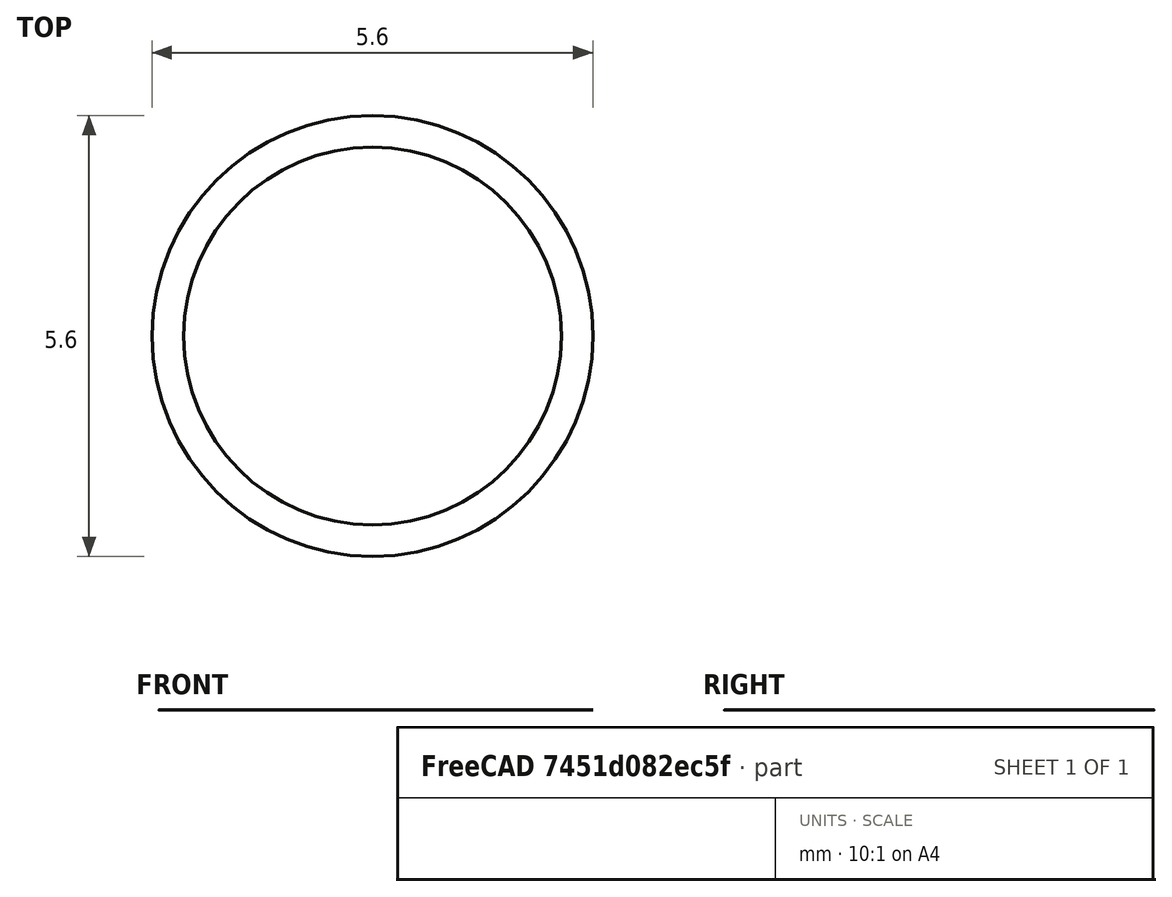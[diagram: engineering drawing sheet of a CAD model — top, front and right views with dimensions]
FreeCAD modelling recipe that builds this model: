
FCSTD DOCUMENT  (FreeCAD 0.20R29603 (Git))
Label: nested_coax
License: All rights reserved
LicenseURL: http://en.wikipedia.org/wiki/All_rights_reserved
objects: Part::Part2DObjectPython×4, App::FeaturePython×4, Part::Cut×1
note: 5 computed .brp shape members not serialized (recipe doc carries the construction recipe); baked Part::Feature solids carry a one-line shape summary decoded from their .brp

FEATURE [Part::Part2DObjectPython] Circle  label="Conductor_0"  # Draft 2D object (typed FeaturePython)
  Area = 50.2655
  FirstAngle = 0
  LastAngle = 0
  MakeFace = true
  Radius = 4
FEATURE [Part::Part2DObjectPython] Circle001  # Draft 2D object (typed FeaturePython)
  Area = 24.6301
  FirstAngle = 0
  LastAngle = 0
  MakeFace = true
  Radius = 2.8
FEATURE [Part::Part2DObjectPython] Circle002  # Draft 2D object (typed FeaturePython)
  Area = 18.0956
  FirstAngle = 0
  LastAngle = 0
  MakeFace = true
  Radius = 2.4
FEATURE [Part::Part2DObjectPython] Circle003  label="Conductor_2"  # Draft 2D object (typed FeaturePython)
  Area = 3.14159
  FirstAngle = 0
  LastAngle = 0
  MakeFace = true
  Radius = 1
FEATURE [Part::Cut] Cut  label="Conductor_1"
  Base = -> Circle001
  Tool = -> Circle002
FEATURE [App::FeaturePython] Dimension001  # Draft dimension (typed FeaturePython)
  Diameter = false
  Dimline = (1.8,4.6,0)
  Direction = (0,0,0)
  Distance = 4.8
  End = (2.4,1e-16,0)
  Normal = (0,0,-1)
  Start = (-2.4,-1e-16,0)
FEATURE [App::FeaturePython] Dimension002  # Draft dimension (typed FeaturePython)
  Diameter = false
  Dimline = (2.8,5,0)
  Direction = (0,0,0)
  Distance = 5.6
  End = (2.8,2e-16,0)
  Normal = (0,0,-1)
  Start = (-2.8,-2e-16,0)
FEATURE [App::FeaturePython] Dimension  # Draft dimension (typed FeaturePython)
  Diameter = false
  Dimline = (0.6,4.2,0)
  Direction = (0,0,0)
  Distance = 2
  End = (1,1e-16,0)
  Normal = (0,0,-1)
  Start = (-1,-1e-16,0)
FEATURE [App::FeaturePython] Dimension003  # Draft dimension (typed FeaturePython)
  Diameter = false
  Dimline = (3.6,5.4,0)
  Direction = (0,0,0)
  Distance = 8
  End = (-4,-2e-16,0)
  Normal = (0,0,-1)
  Start = (4,2e-16,0)
